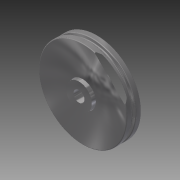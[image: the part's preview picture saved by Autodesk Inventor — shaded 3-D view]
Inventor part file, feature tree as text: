
AUTODESK INVENTOR PART (.ipt)
format: ipt  version: 2015 SP1 (Build 190203100, 203)  size: 182,784 bytes
history: native  units: in
note: dims shown in document units (in); Inventor stores cm internally (conversion verified against a paired STEP export)
features: extrude x4, sketch x4, plane x1, fillet x1, projected_geometry x1
ambient origin geometry x8: Origin, YZ Plane, XZ Plane, XY Plane, X Axis, Y Axis, Z Axis, Center Point
bodies: Solid1 (feature_tree)
feature tree (11):
  extrude  "Extrusion1"  Depth=3.0in
  plane  "Work Plane1"
  extrude  "Extrusion3"  Depth=0.5in
  extrude  "Extrusion4"  Depth=0.75in
  extrude  "Extrusion5"  Depth=0.125in
  fillet  "Fillet2"  [1 undecoded]
  sketch  "Sketch1"  dims[d0=0.9in d1=3.0in]
  sketch  "Sketch3"  dims[d2=0.5in d3=0.0in d9=0.875in]
  sketch  "Sketch4"  dims[d10=0.75in d11=0.0in d12=0.375in]
  sketch  "Sketch5"  dims[d13=1.0in d14=0.0in d15=0.125in d16=0.0in d17=0.125in d18=0.0in d19=0.0312in]
  projected_geometry  "Projected Loop1"
note: 1 required parameter value undecoded (feature->parameter linkage not recoverable at this tier; creation-order binding heuristic only, values carry confidence <= 0.55)
